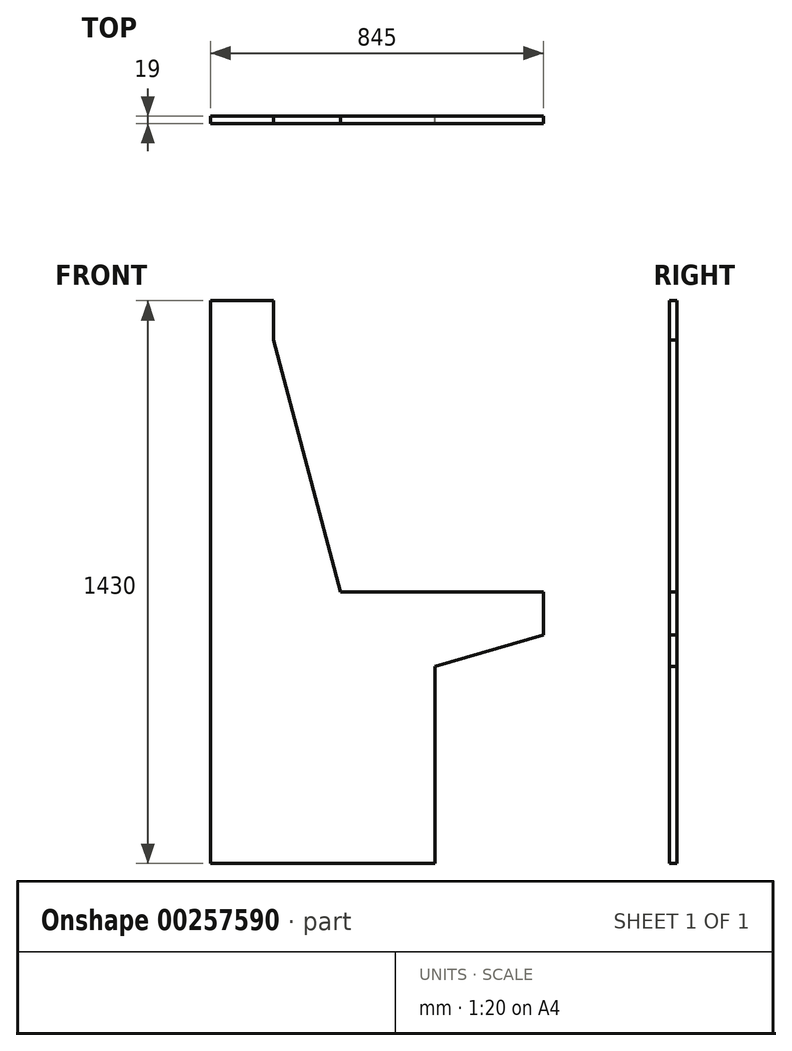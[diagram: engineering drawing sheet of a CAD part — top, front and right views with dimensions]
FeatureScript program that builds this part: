
annotation { "Feature Type Name" : "Feature", "Feature Type Description" : "" }
export const myFeature = defineFeature(function(context is Context, id is Id, definition is map)
    precondition{}
    {
        {
            var Q0;
            Q0=qCreatedBy(makeId("Front.planeOp"),FACE);
            var sketch = newSketch(context, id + "F0", { "sketchPlane" : qUnion([Q0])});
            skLineSegment(sketch, "E0", {"start": v(0, 0) * mm, "end": v(0, 1430) * mm});
            skLineSegment(sketch, "E1", {"start": v(0, 1430) * mm, "end": v(160, 1430) * mm});
            skLineSegment(sketch, "E2", {"start": v(160, 1430) * mm, "end": v(160, 1330) * mm});
            skLineSegment(sketch, "E3", {"start": v(160, 1330) * mm, "end": v(330, 690) * mm});
            skLineSegment(sketch, "E4", {"start": v(330, 690) * mm, "end": v(845, 690) * mm});
            skLineSegment(sketch, "E5", {"start": v(845, 690) * mm, "end": v(845, 580) * mm});
            skLineSegment(sketch, "E6", {"start": v(845, 580) * mm, "end": v(570, 500) * mm});
            skLineSegment(sketch, "E7", {"start": v(570, 500) * mm, "end": v(570, 0) * mm});
            skLineSegment(sketch, "E8", {"start": v(570, 0) * mm, "end": v(0, 0) * mm});
            skSolve(sketch);
        }
        {
            var Q0;
            Q0=makeQuery(id+"F0.imprint","IMPRINT",FACE,{"disambiguationData":[TD([[makeQuery(id+"F0.imprint","IMPRINT",EDGE,{"derivedFrom":sQuery(id+"F0.wireOp",EDGE,"E0")}),-1.0]])]});
            extrude(context, id + "F1", {"entities" : qUnion([Q0]), "depth" : 19 * mm});
        }
    });
